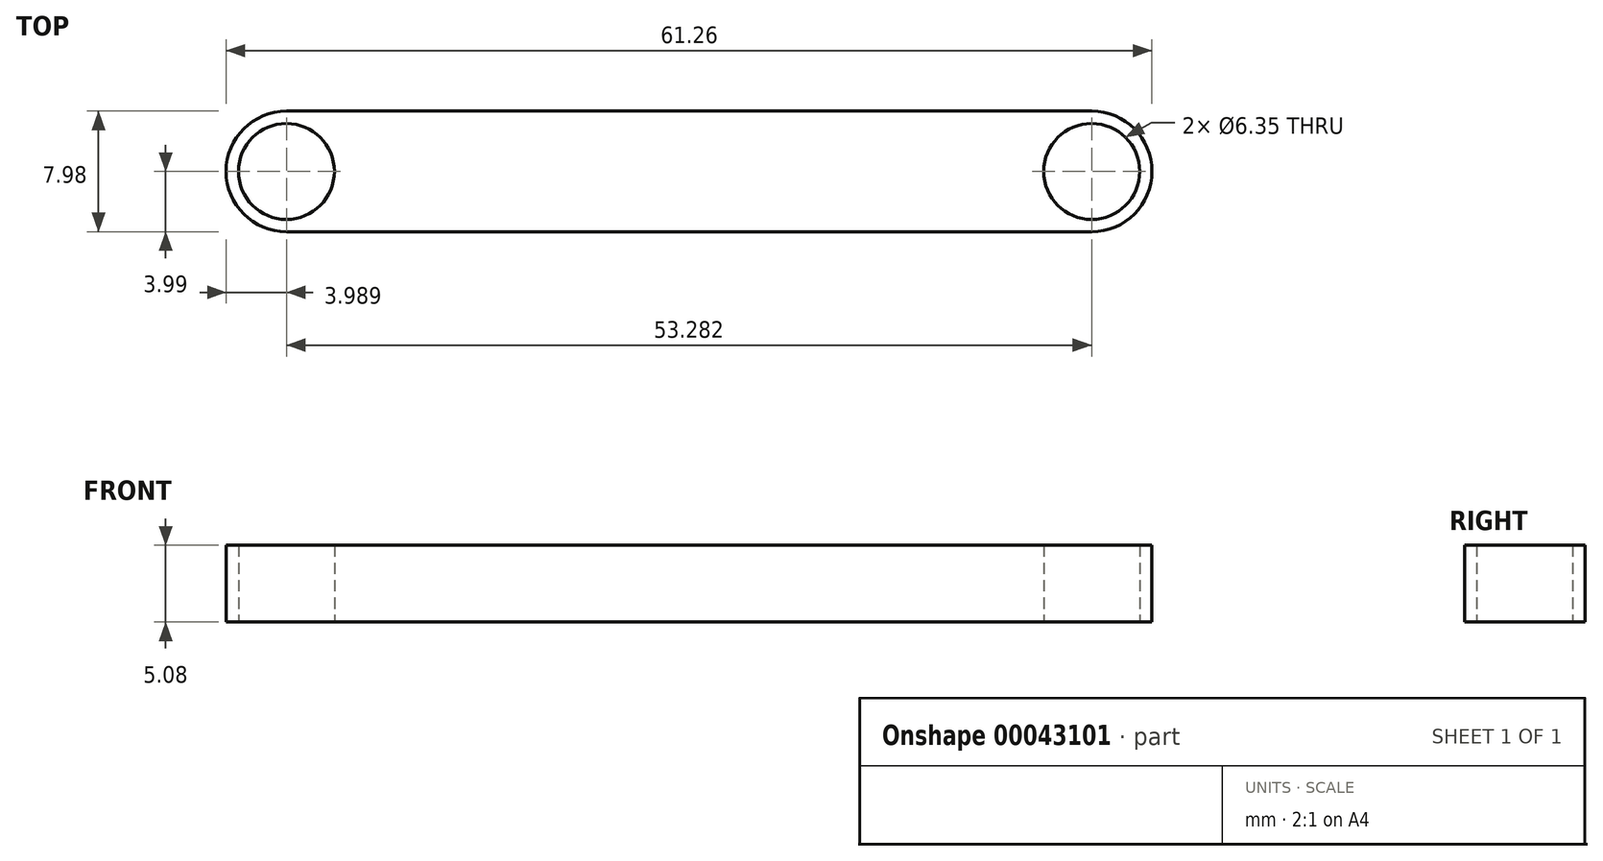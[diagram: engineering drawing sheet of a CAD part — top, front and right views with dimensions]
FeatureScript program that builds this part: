
annotation { "Feature Type Name" : "Feature", "Feature Type Description" : "" }
export const myFeature = defineFeature(function(context is Context, id is Id, definition is map)
    precondition{}
    {
        {
            var Q0;
            Q0=qCreatedBy(makeId("Top.planeOp"),FACE);
            var sketch = newSketch(context, id + "F0", { "sketchPlane" : qUnion([Q0])});
            skLineSegment(sketch, "E0.bottom", {"start": v(-26.64, 4) * mm, "end": v(0, 4) * mm});
            skLineSegment(sketch, "E0.left", {"start": v(-26.64, 4) * mm, "end": v(-26.64, 0) * mm});
            skLineSegment(sketch, "E1.MirrorCS", {"start": v(26.64, 4) * mm, "end": v(26.64, 0) * mm});
            skLineSegment(sketch, "E2.MirrorCS", {"start": v(26.64, 4) * mm, "end": v(0, 4) * mm});
            skLineSegment(sketch, "E3.MirrorCS", {"start": v(26.64, -4) * mm, "end": v(0, -4) * mm});
            skLineSegment(sketch, "E4.MirrorCS", {"start": v(-26.64, -4) * mm, "end": v(0, -4) * mm});
            skLineSegment(sketch, "E5.MirrorCS", {"start": v(-26.64, -4) * mm, "end": v(-26.64, 0) * mm});
            skLineSegment(sketch, "E6.MirrorCS", {"start": v(26.64, -4) * mm, "end": v(26.64, 0) * mm});
            skArc(sketch, "E7", {"start": v(-26.64, 4) * mm, "mid": v(-30.63, 0) * mm, "end": v(-26.64, -4) * mm});
            skArc(sketch, "E8", {"start": v(26.64, -4) * mm, "mid": v(30.63, 0) * mm, "end": v(26.64, 4) * mm});
            skCircle(sketch, "E9", {"center": v(26.64, 0) * mm, "radius": 3.18 * mm});
            skCircle(sketch, "E10", {"center": v(-26.64, 0) * mm, "radius": 3.18 * mm});
            skSolve(sketch);
        }
        {
            var Q0;
            Q0 = qSketchRegion(id + "F0", true);
            extrude(context, id + "F1", {"entities" : qUnion([Q0]), "depth" : 5.08 * mm});
        }
    });
